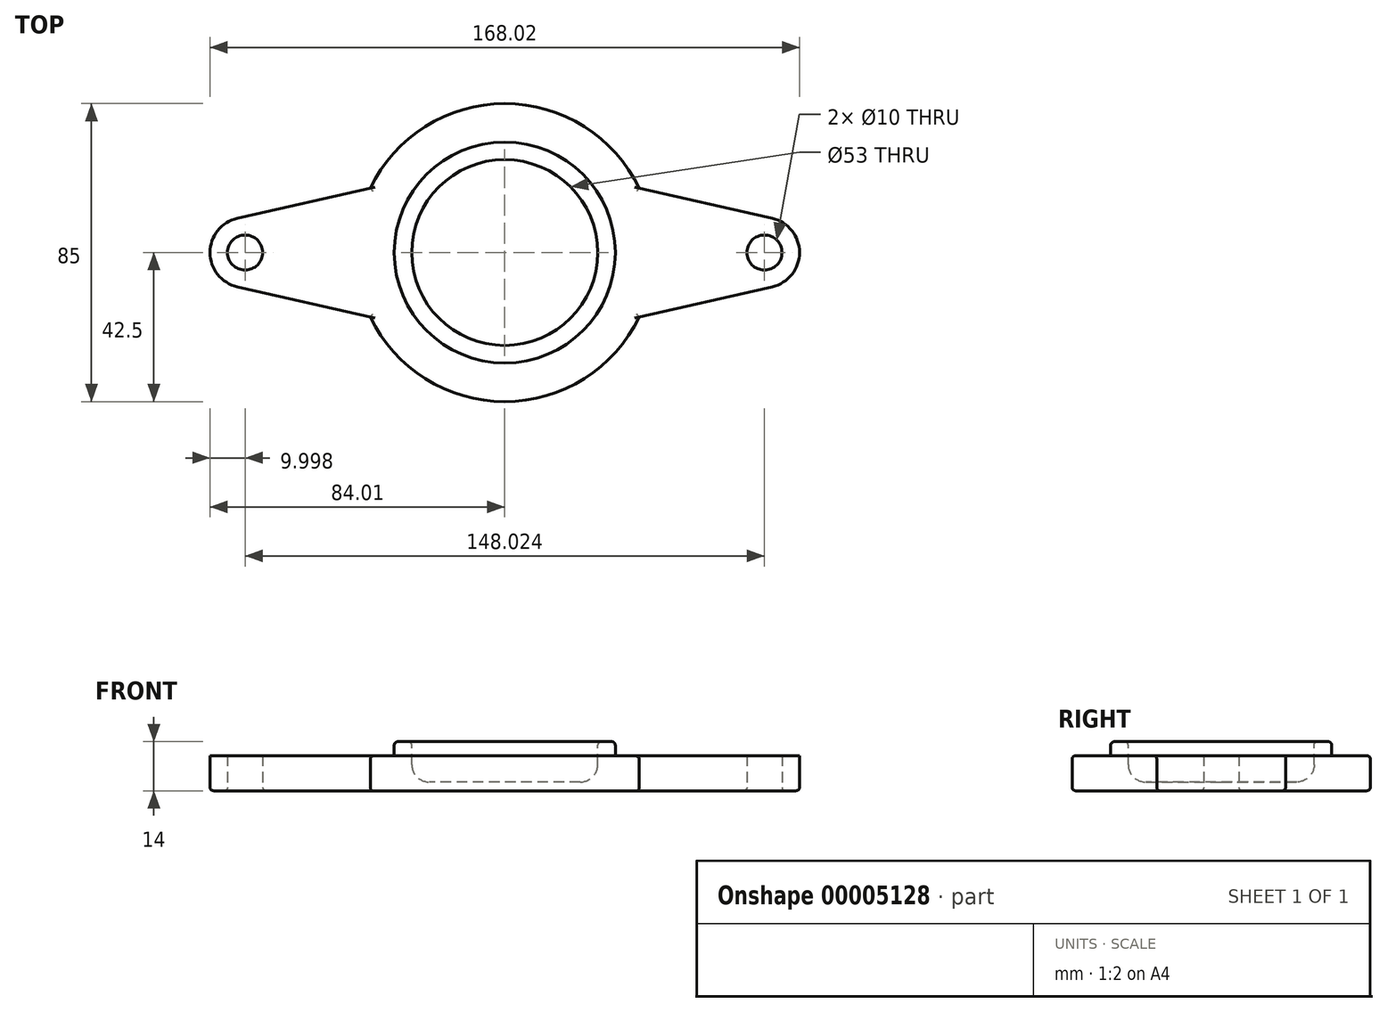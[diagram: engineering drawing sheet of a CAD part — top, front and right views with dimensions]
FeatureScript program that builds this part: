
annotation { "Feature Type Name" : "Feature", "Feature Type Description" : "" }
export const myFeature = defineFeature(function(context is Context, id is Id, definition is map)
    precondition{}
    {
        {
            var Q0;
            Q0=qCreatedBy(makeId("Right.planeOp"),FACE);
            var sketch = newSketch(context, id + "F0", { "sketchPlane" : qUnion([Q0])});
            skLineSegment(sketch, "E0.bottom", {"start": v(-41.5, 5) * mm, "end": v(-31.5, 5) * mm});
            skLineSegment(sketch, "E0.top", {"start": v(-41.5, -5) * mm, "end": v(0, -5) * mm});
            skLineSegment(sketch, "E0.left", {"start": v(-42.5, 4) * mm, "end": v(-42.5, -4) * mm});
            skLineSegment(sketch, "E1", {"start": v(0, 5) * mm, "end": v(0, -5) * mm, "construction": true});
            skLineSegment(sketch, "E2.top", {"start": v(-30.5, 9) * mm, "end": v(-27.5, 9) * mm});
            skLineSegment(sketch, "E2.left", {"start": v(-31.5, 5) * mm, "end": v(-31.5, 8) * mm});
            skLineSegment(sketch, "E2.right", {"start": v(-26.5, 6.16) * mm, "end": v(-26.5, 8) * mm});
            skLineSegment(sketch, "E3", {"start": v(-26.5, 6.16) * mm, "end": v(0, 6.16) * mm, "construction": true});
            skLineSegment(sketch, "E4", {"start": v(0, 5) * mm, "end": v(0, 6.16) * mm, "construction": true});
            skLineSegment(sketch, "E5.top", {"start": v(-21.5, -2.5) * mm, "end": v(0, -2.5) * mm});
            skLineSegment(sketch, "E5.left", {"start": v(-26.5, 6.16) * mm, "end": v(-26.5, 2.5) * mm});
            skPoint(sketch, "E6.visualSharp", {"position": v(-31.5, 9) * mm});
            skArc(sketch, "E6.filletArc", {"start": v(-30.5, 9) * mm, "mid": v(-31.2, 8.7) * mm, "end": v(-31.5, 8) * mm});
            skPoint(sketch, "E7.visualSharp", {"position": v(-26.5, 9) * mm});
            skArc(sketch, "E7.filletArc", {"start": v(-26.5, 8) * mm, "mid": v(-26.8, 8.7) * mm, "end": v(-27.5, 9) * mm});
            skLineSegment(sketch, "E8", {"start": v(0, -2.5) * mm, "end": v(0, -5) * mm});
            skPoint(sketch, "E9.visualSharp", {"position": v(-42.5, 5) * mm});
            skArc(sketch, "E9.filletArc", {"start": v(-41.5, 5) * mm, "mid": v(-42.2, 4.7) * mm, "end": v(-42.5, 4) * mm});
            skPoint(sketch, "E10.visualSharp", {"position": v(-42.5, -5) * mm});
            skArc(sketch, "E10.filletArc", {"start": v(-42.5, -4) * mm, "mid": v(-42.2, -4.7) * mm, "end": v(-41.5, -5) * mm});
            skPoint(sketch, "E11.visualSharp", {"position": v(-26.5, -2.5) * mm});
            skArc(sketch, "E11.filletArc", {"start": v(-26.5, 2.5) * mm, "mid": v(-25.04, -1.04) * mm, "end": v(-21.5, -2.5) * mm});
            skSolve(sketch);
        }
        {
            var Q0;
            Q0=makeQuery(id+"F0.imprint","IMPRINT",FACE,{"disambiguationData":[TD([[makeQuery(id+"F0.imprint","IMPRINT",EDGE,{"derivedFrom":sQuery(id+"F0.wireOp",EDGE,"E0.bottom")}),-1.0]])]});
            var Q1;
            Q1=sQuery(id+"F0.wireOp",EDGE,"E1");
            revolve(context, id + "F1", {"entities" : qUnion([Q0]), "axis" : qUnion([Q1]), "revolveType" : RevolveType.FULL});
        }
        {
            var Q0;
            Q0=qCreatedBy(makeId("Top.planeOp"),FACE);
            cPlane(context, id + "F2", {"entities" : qUnion([Q0]), "cplaneType" : CPlaneType.OFFSET, "offset" : 5 * mm, "oppositeDirection" : true, "width" : 150 * mm, "height" : 150 * mm});
        }
        {
            var Q0;
            Q0=qCreatedBy(id+"F2.planeOp",FACE);
            var sketch = newSketch(context, id + "F3", { "sketchPlane" : qUnion([Q0])});
            skLineSegment(sketch, "E12", {"start": v(0, 0) * mm, "end": v(-74.01, 0) * mm, "construction": true});
            skArc(sketch, "E13", {"start": v(-76.23, 9.75) * mm, "mid": v(-84.01, 0) * mm, "end": v(-76.23, -9.75) * mm});
            skLineSegment(sketch, "E14", {"start": v(-76.23, -9.75) * mm, "end": v(-34.98, -19.14) * mm});
            skLineSegment(sketch, "E15", {"start": v(-34.98, -19.14) * mm, "end": v(-34.98, 19.14) * mm});
            skLineSegment(sketch, "E16", {"start": v(-34.98, 19.14) * mm, "end": v(-76.23, 9.75) * mm});
            skPoint(sketch, "E17", {"position": v(-34.98, 0) * mm});
            skCircle(sketch, "E18", {"center": v(-74.01, 0) * mm, "radius": 5 * mm});
            skSolve(sketch);
        }
        {
            var Q0;
            Q0 = qSketchRegion(id + "F3", true);
            var Q1;
            Q1=makeQuery(id+"F1.opRevolve","SWEPT_FACE",FACE,{"disambiguationData":[OSD([sQuery(id+"F0.wireOp",EDGE,"E0.bottom")])]});
            extrude(context, id + "F4", {"entities" : qUnion([Q0]), "endBound" : BoundingType.UP_TO_SURFACE, "endBoundEntityFace" : qUnion([Q1]), "depth" : 25 * mm});
        }
        {
            var Q0;
            Q0=makeQuery(id+"F4.opExtrude","SWEPT_BODY",BODY,{"disambiguationData":[OSD([sQuery(id+"F3.wireOp",EDGE,"E13"),sQuery(id+"F3.wireOp",EDGE,"E14"),sQuery(id+"F3.wireOp",EDGE,"E15"),sQuery(id+"F3.wireOp",EDGE,"E16"),sQuery(id+"F3.wireOp",EDGE,"E18")])]});
            var Q1;
            Q1=qCreatedBy(makeId("Right.planeOp"),FACE);
            mirror(context, id + "F5", {"entities" : qUnion([Q0]), "mirrorPlane" : qUnion([Q1])});
        }
        {
            var Q0;
            Q0=makeQuery(id+"F4.opExtrude","SWEPT_BODY",BODY,{"disambiguationData":[OSD([sQuery(id+"F3.wireOp",EDGE,"E13"),sQuery(id+"F3.wireOp",EDGE,"E14"),sQuery(id+"F3.wireOp",EDGE,"E15"),sQuery(id+"F3.wireOp",EDGE,"E16"),sQuery(id+"F3.wireOp",EDGE,"E18")])]});
            var Q1;
            Q1=makeQuery(id+"F1.opRevolve","SWEPT_BODY",BODY,{"disambiguationData":[OSD([sQuery(id+"F0.wireOp",EDGE,"E0.bottom"),sQuery(id+"F0.wireOp",EDGE,"E0.top"),sQuery(id+"F0.wireOp",EDGE,"E0.left"),sQuery(id+"F0.wireOp",EDGE,"E2.top"),sQuery(id+"F0.wireOp",EDGE,"E2.left"),sQuery(id+"F0.wireOp",EDGE,"E2.right"),sQuery(id+"F0.wireOp",EDGE,"E5.top"),sQuery(id+"F0.wireOp",EDGE,"E5.left"),sQuery(id+"F0.wireOp",EDGE,"E6.filletArc"),sQuery(id+"F0.wireOp",EDGE,"E7.filletArc"),sQuery(id+"F0.wireOp",EDGE,"E8"),sQuery(id+"F0.wireOp",EDGE,"E9.filletArc"),sQuery(id+"F0.wireOp",EDGE,"E10.filletArc"),sQuery(id+"F0.wireOp",EDGE,"E11.filletArc")])]});
            var Q2;
            Q2=makeQuery(id+"F5.opPattern","COPY",BODY,{"derivedFrom":makeQuery(id+"F4.opExtrude","SWEPT_BODY",BODY,{"disambiguationData":[OSD([sQuery(id+"F3.wireOp",EDGE,"E13"),sQuery(id+"F3.wireOp",EDGE,"E14"),sQuery(id+"F3.wireOp",EDGE,"E15"),sQuery(id+"F3.wireOp",EDGE,"E16"),sQuery(id+"F3.wireOp",EDGE,"E18")])]}),"instanceName":"1"});
            booleanBodies(context, id + "F6", {"operationType" : BooleanOperationType.UNION, "tools" : qUnion([Q0, Q1, Q2])});
        }
        {
            var Q0;
            Q0=makeQuery(id+"F4.opExtrude","CAP_EDGE",EDGE,{"disambiguationData":[OSD([sQuery(id+"F3.wireOp",EDGE,"E14")])],"isStart":true});
            var Q1;
            {var subQ0=makeQuery(id+"F4.opExtrude","CAP_FACE",FACE,{"disambiguationData":[OSD([sQuery(id+"F3.wireOp",EDGE,"E13"),sQuery(id+"F3.wireOp",EDGE,"E14"),sQuery(id+"F3.wireOp",EDGE,"E15"),sQuery(id+"F3.wireOp",EDGE,"E16"),sQuery(id+"F3.wireOp",EDGE,"E18")])],"isStart":true});Q1=makeQuery(id+"F6.opBoolean","MERGE",FACE,{"derivedFrom":[makeQuery(id+"F1.opRevolve","SWEPT_FACE",FACE,{"disambiguationData":[OSD([sQuery(id+"F0.wireOp",EDGE,"E0.top")])]}),subQ0,makeQuery(id+"F5.opPattern","COPY",FACE,{"derivedFrom":subQ0,"instanceName":"1"})]});}
            fillet(context, id + "F7", {"entities" : qUnion([Q0, Q1]), "radius" : 1 * mm, "tangentPropagation" : true, "allowEdgeOverflow" : false});
        }
    });
